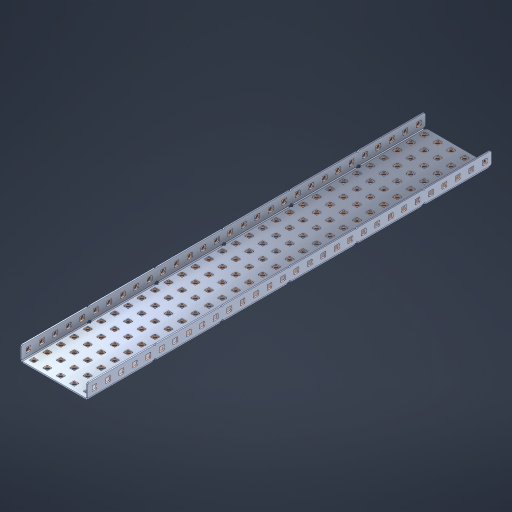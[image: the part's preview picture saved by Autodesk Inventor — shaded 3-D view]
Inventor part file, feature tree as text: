
AUTODESK INVENTOR PART (.ipt)
format: ipt  version: 2023 (Build 270158000, 158)  size: 2,276,864 bytes
history: native  units: in
note: dims shown in document units (in); Inventor stores cm internally (conversion verified against a paired STEP export)
features: other x215, extrude x209, sheet_metal_op x10, sketch x8, mirror x1, pattern_linear x1, chamfer x1
ambient origin geometry x8: Origin, YZ Plane, XZ Plane, XY Plane, X Axis, Y Axis, Z Axis, Center Point
bodies: Solid1 (feature_tree), Body (feature_tree)
feature tree (445):
  other  "Flange Pattern Plane"
  sheet_metal_op  "Flange Pattern"
  sheet_metal_op  "Body Pattern"
  other  "Arc Length"
  mirror  "Notch Mirror"
  pattern_linear  "Notch Pattern"  Spacing1=0.1875in  [1 undecoded]
  chamfer  "End Chamfer"
  extrude  "Half Cut"  Depth=0.0469in
  sketch  "Sketch1"  dims[d0=2.5in]
  other  "Plate1"
  sketch  "Sketch2"  dims[d1=15.0in]
  other  "Plate2"
  sheet_metal_op  "Bend1"
  sheet_metal_op  "Corner1"
  sketch  "Sketch3"  dims[d2=0.0469in]
  other  "Flange Pattern Sketch"
  sketch  "Sketch7"  dims[d3=0.0469in]
  other  "Srf1"
  other  "Srf2"
  sketch  "Sketch8"  dims[d4=0.0234in]
  sketch  "Sketch9"  dims[d5=0.0938in]
  other  "Srf91"
  sheet_metal_op  "Body Pattern Sketch"
  other  "Srf92"
  sketch  "Sketch13"  dims[d6=0.0469in]
  sketch  "Sketch14"  dims[d7=0.5in d8=90.0deg d9=0.0312in d10=0.1875in d11=0.0469in d12=0.0469in d16=0.182in d17=0.02in d18=0.0469in d19=0.0in d20=0.25in d21=0.25in d46=0.172in d47=1.0in d48=0.0in d49=0.182in d50=0.02in d51=0.25in d52=0.25in d53=0.0469in d54=0.0in d55=0.172in d56=1.0in d57=0.0in d60=11.811in d62=0.5in d63=1.9685in d65=0.5in d85=0.1227in d86=0.1659in d88=0.04in d89=0.0469in d90=0.0in d91=0.04in d92=0.0491in d95=2.5in d96=0.04in d97=0.25in d98=45.0deg d101=0.0in d102=2.497in d131=2.5in d132=11.811in d134=0.5in d139=0.5in]
  other  "Srf856"
  other  "Srf1310"
  other  "Srf1311"
  other  "Srf1312"
  other  "Srf1376"
  other  "Srf1377"
  other  "Srf1728"
  other  "Srf1755"
  other  "Srf1878"
  other  "Srf1879"
  other  "Srf1880"
  other  "Srf1881"
  other  "Srf1882"
  other  "Srf1883"
  other  "Srf1884"
  other  "Srf1885"
  other  "Srf1886"
  other  "Srf1887"
  other  "Srf1888"
  other  "Srf1889"
  other  "Srf1890"
  other  "Srf1891"
  other  "Srf1892"
  other  "Srf1893"
  other  "Srf1894"
  other  "Srf1895"
  other  "Srf1896"
  other  "Srf1897"
  other  "Srf1898"
  other  "Srf1899"
  other  "Srf1900"
  other  "Srf1901"
  other  "Srf1902"
  other  "Srf1903"
  other  "Srf1904"
  other  "Srf1905"
  other  "Srf1906"
  other  "Srf1942"
  other  "Srf1943"
  other  "Srf1944"
  other  "Srf1945"
  other  "Srf1946"
  other  "Srf1947"
  other  "Srf1948"
  other  "Srf1949"
  other  "Srf1950"
  other  "Srf1951"
  other  "Srf1952"
  other  "Srf1953"
  other  "Srf1954"
  other  "Srf1955"
  other  "Srf1956"
  other  "Srf1957"
  other  "Srf1958"
  other  "Srf1959"
  other  "Srf1960"
  other  "Srf1961"
  other  "Srf1962"
  other  "Srf1963"
  other  "Srf1964"
  other  "Srf1965"
  other  "Srf1966"
  other  "Srf1967"
  other  "Srf1968"
  other  "Srf1969"
  other  "Srf1970"
  other  "Srf2111"
  other  "Srf2112"
  other  "Srf2113"
  other  "Srf2114"
  other  "Srf2115"
  other  "Srf2116"
  other  "Srf2117"
  other  "Srf2118"
  other  "Srf2119"
  other  "Srf2120"
  other  "Srf2121"
  other  "Srf2122"
  other  "Srf2123"
  other  "Srf2124"
  other  "Srf2125"
  other  "Srf2126"
  other  "Srf2127"
  other  "Srf2128"
  other  "Srf2129"
  other  "Srf2130"
  other  "Srf2131"
  other  "Srf2132"
  other  "Srf2133"
  other  "Srf2134"
  other  "Srf2135"
  other  "Srf2146"
  other  "Srf2147"
  other  "Srf2148"
  other  "Srf2149"
  other  "Srf2150"
  other  "Srf2151"
  other  "Srf2152"
  other  "Srf2153"
  other  "Srf2154"
  other  "Srf2155"
  other  "Srf2156"
  other  "Srf2157"
  other  "Srf2158"
  other  "Srf2159"
  other  "Srf2160"
  other  "Srf2161"
  other  "Srf2162"
  other  "Srf2163"
  other  "Srf2164"
  other  "Srf2165"
  other  "Srf2166"
  other  "Srf2167"
  other  "Srf2168"
  other  "Srf2169"
  other  "Srf2170"
  other  "Srf2171"
  other  "Srf2172"
  other  "Srf2173"
  other  "Srf2174"
  other  "Srf2175"
  other  "Srf2176"
  other  "Srf2177"
  other  "Srf2178"
  other  "Srf2179"
  other  "Srf2180"
  other  "Srf2181"
  other  "Srf2182"
  other  "Srf2183"
  other  "Srf2184"
  other  "Srf2185"
  other  "Srf2186"
  other  "Srf2187"
  other  "Srf2188"
  other  "Srf2189"
  other  "Srf2190"
  other  "Srf2191"
  other  "Srf2192"
  other  "Srf2193"
  other  "Srf2194"
  other  "Srf2195"
  other  "Srf2196"
  other  "Srf2197"
  other  "Srf2198"
  other  "Srf2199"
  other  "Srf2200"
  other  "Srf2201"
  other  "Srf2202"
  other  "Srf2203"
  other  "Srf2204"
  other  "Srf2205"
  other  "Srf2206"
  other  "Srf2207"
  other  "Srf2208"
  other  "Srf2209"
  other  "Srf2210"
  other  "Srf2211"
  other  "Srf2212"
  other  "Srf2213"
  other  "Srf2214"
  other  "Srf2215"
  other  "Srf2216"
  other  "Srf2217"
  other  "Srf2218"
  other  "Srf2219"
  other  "Srf2220"
  other  "Srf2221"
  other  "Srf2222"
  other  "Srf2223"
  other  "Srf2224"
  other  "Srf2225"
  other  "Srf2226"
  other  "Srf2227"
  other  "Srf2228"
  other  "Srf2229"
  other  "Srf2230"
  other  "Srf2231"
  other  "Srf2232"
  other  "Srf2233"
  other  "Srf2234"
  other  "Srf2235"
  other  "Srf2236"
  other  "Srf2237"
  other  "Srf2238"
  other  "Srf2239"
  other  "Srf2240"
  other  "Srf2241"
  other  "Srf2242"
  other  "Srf2243"
  other  "Srf2244"
  other  "Srf2245"
  other  "Srf2246"
  other  "Srf2247"
  other  "Srf2248"
  other  "Srf2249"
  other  "Srf2250"
  other  "Srf2251"
  other  "Srf2252"
  other  "Srf2253"
  other  "Srf2254"
  other  "Srf2255"
  other  "Srf2256"
  other  "Srf2257"
  other  "Srf2258"
  other  "Srf2259"
  other  "Srf2260"
  sheet_metal_op  "Flange Stamp"
  sheet_metal_op  "Flange Circle"
  sheet_metal_op  "Body Stamp"
  sheet_metal_op  "Body Circle"
  sheet_metal_op  "Notch"
  extrude  "ExtrusionSrf2"  Depth=0.0469in
  extrude  "ExtrusionSrf92"  Depth=2.5in
  extrude  "ExtrusionSrf856"  Depth=0.02in
  extrude  "ExtrusionSrf1310"  Depth=0.0469in
  extrude  "ExtrusionSrf1311"  TaperAngle=0.0deg  [1 undecoded]
  extrude  "ExtrusionSrf1312"  Depth=0.25in
  extrude  "ExtrusionSrf1376"  Depth=0.25in
  extrude  "ExtrusionSrf1377"  Depth=2.5in
  extrude  "ExtrusionSrf1728"  Depth=2.5in TaperAngle=0.0deg
  extrude  "ExtrusionSrf1755"  Depth=2.5in
  extrude  "ExtrusionSrf1878"  Depth=0.02in
  extrude  "ExtrusionSrf1879"  Depth=0.25in
  extrude  "ExtrusionSrf1880"  Depth=0.25in
  extrude  "ExtrusionSrf1881"  Depth=0.0469in
  extrude  "ExtrusionSrf1882"  TaperAngle=0.0deg  [1 undecoded]
  extrude  "ExtrusionSrf1883"  Depth=2.5in
  extrude  "ExtrusionSrf1884"  Depth=2.5in TaperAngle=0.0deg
  extrude  "ExtrusionSrf1885"  Depth=2.5in
  extrude  "ExtrusionSrf1886"  Depth=2.5in
  extrude  "ExtrusionSrf1887"  Depth=2.5in
  extrude  "ExtrusionSrf1888"  Depth=2.5in
  extrude  "ExtrusionSrf1889"  Depth=2.5in
  extrude  "ExtrusionSrf1890"  Depth=0.0469in
  extrude  "ExtrusionSrf1891"  TaperAngle=0.0deg  [1 undecoded]
  extrude  "ExtrusionSrf1892"  Depth=2.5in
  extrude  "ExtrusionSrf1893"  Depth=2.5in
  extrude  "ExtrusionSrf1894"  Depth=2.5in
  extrude  "ExtrusionSrf1895"  Depth=0.25in TaperAngle=45.0deg
  extrude  "ExtrusionSrf1896"  TaperAngle=0.0deg  [1 undecoded]
  extrude  "ExtrusionSrf1897"  Depth=2.5in
  extrude  "ExtrusionSrf1898"  Depth=2.5in
  extrude  "ExtrusionSrf1899"  Depth=2.5in
  extrude  "ExtrusionSrf1900"  Depth=2.5in
  extrude  "ExtrusionSrf1901"  Depth=2.5in
  extrude  "ExtrusionSrf1902"  [1 undecoded]
  extrude  "ExtrusionSrf1903"  [1 undecoded]
  extrude  "ExtrusionSrf1904"  [1 undecoded]
  extrude  "ExtrusionSrf1905"  [1 undecoded]
  extrude  "ExtrusionSrf1906"  [1 undecoded]
  extrude  "ExtrusionSrf1942"  [1 undecoded]
  extrude  "ExtrusionSrf1943"  [1 undecoded]
  extrude  "ExtrusionSrf1944"  [1 undecoded]
  extrude  "ExtrusionSrf1945"  [1 undecoded]
  extrude  "ExtrusionSrf1946"  [1 undecoded]
  extrude  "ExtrusionSrf1947"  [1 undecoded]
  extrude  "ExtrusionSrf1948"  [1 undecoded]
  extrude  "ExtrusionSrf1949"  [1 undecoded]
  extrude  "ExtrusionSrf1950"  [1 undecoded]
  extrude  "ExtrusionSrf1951"  [1 undecoded]
  extrude  "ExtrusionSrf1952"  [1 undecoded]
  extrude  "ExtrusionSrf1953"  [1 undecoded]
  extrude  "ExtrusionSrf1954"  [1 undecoded]
  extrude  "ExtrusionSrf1955"  [1 undecoded]
  extrude  "ExtrusionSrf1956"  [1 undecoded]
  extrude  "ExtrusionSrf1957"  [1 undecoded]
  extrude  "ExtrusionSrf1958"  [1 undecoded]
  extrude  "ExtrusionSrf1959"  [1 undecoded]
  extrude  "ExtrusionSrf1960"  [1 undecoded]
  extrude  "ExtrusionSrf1961"  [1 undecoded]
  extrude  "ExtrusionSrf1962"  [1 undecoded]
  extrude  "ExtrusionSrf1963"  [1 undecoded]
  extrude  "ExtrusionSrf1964"  [1 undecoded]
  extrude  "ExtrusionSrf1965"  [1 undecoded]
  extrude  "ExtrusionSrf1966"  [1 undecoded]
  extrude  "ExtrusionSrf1967"  [1 undecoded]
  extrude  "ExtrusionSrf1968"  [1 undecoded]
  extrude  "ExtrusionSrf1969"  [1 undecoded]
  extrude  "ExtrusionSrf1970"  [1 undecoded]
  extrude  "ExtrusionSrf2111"  [1 undecoded]
  extrude  "ExtrusionSrf2112"  [1 undecoded]
  extrude  "ExtrusionSrf2113"  [1 undecoded]
  extrude  "ExtrusionSrf2114"  [1 undecoded]
  extrude  "ExtrusionSrf2115"  [1 undecoded]
  extrude  "ExtrusionSrf2116"  [1 undecoded]
  extrude  "ExtrusionSrf2117"  [1 undecoded]
  extrude  "ExtrusionSrf2118"  [1 undecoded]
  extrude  "ExtrusionSrf2119"  [1 undecoded]
  extrude  "ExtrusionSrf2120"  [1 undecoded]
  extrude  "ExtrusionSrf2121"  [1 undecoded]
  extrude  "ExtrusionSrf2122"  [1 undecoded]
  extrude  "ExtrusionSrf2123"  [1 undecoded]
  extrude  "ExtrusionSrf2124"  [1 undecoded]
  extrude  "ExtrusionSrf2125"  [1 undecoded]
  extrude  "ExtrusionSrf2126"  [1 undecoded]
  extrude  "ExtrusionSrf2127"  [1 undecoded]
  extrude  "ExtrusionSrf2128"  [1 undecoded]
  extrude  "ExtrusionSrf2129"  [1 undecoded]
  extrude  "ExtrusionSrf2130"  [1 undecoded]
  extrude  "ExtrusionSrf2131"  [1 undecoded]
  extrude  "ExtrusionSrf2132"  [1 undecoded]
  extrude  "ExtrusionSrf2133"  [1 undecoded]
  extrude  "ExtrusionSrf2134"  [1 undecoded]
  extrude  "ExtrusionSrf2135"  [1 undecoded]
  extrude  "ExtrusionSrf2146"  [1 undecoded]
  extrude  "ExtrusionSrf2147"  [1 undecoded]
  extrude  "ExtrusionSrf2148"  [1 undecoded]
  extrude  "ExtrusionSrf2149"  [1 undecoded]
  extrude  "ExtrusionSrf2150"  [1 undecoded]
  extrude  "ExtrusionSrf2151"  [1 undecoded]
  extrude  "ExtrusionSrf2152"  [1 undecoded]
  extrude  "ExtrusionSrf2153"  [1 undecoded]
  extrude  "ExtrusionSrf2154"  [1 undecoded]
  extrude  "ExtrusionSrf2155"  [1 undecoded]
  extrude  "ExtrusionSrf2156"  [1 undecoded]
  extrude  "ExtrusionSrf2157"  [1 undecoded]
  extrude  "ExtrusionSrf2158"  [1 undecoded]
  extrude  "ExtrusionSrf2159"  [1 undecoded]
  extrude  "ExtrusionSrf2160"  [1 undecoded]
  extrude  "ExtrusionSrf2161"  [1 undecoded]
  extrude  "ExtrusionSrf2162"  [1 undecoded]
  extrude  "ExtrusionSrf2163"  [1 undecoded]
  extrude  "ExtrusionSrf2164"  [1 undecoded]
  extrude  "ExtrusionSrf2165"  [1 undecoded]
  extrude  "ExtrusionSrf2166"  [1 undecoded]
  extrude  "ExtrusionSrf2167"  [1 undecoded]
  extrude  "ExtrusionSrf2168"  [1 undecoded]
  extrude  "ExtrusionSrf2169"  [1 undecoded]
  extrude  "ExtrusionSrf2170"  [1 undecoded]
  extrude  "ExtrusionSrf2171"  [1 undecoded]
  extrude  "ExtrusionSrf2172"  [1 undecoded]
  extrude  "ExtrusionSrf2173"  [1 undecoded]
  extrude  "ExtrusionSrf2174"  [1 undecoded]
  extrude  "ExtrusionSrf2175"  [1 undecoded]
  extrude  "ExtrusionSrf2176"  [1 undecoded]
  extrude  "ExtrusionSrf2177"  [1 undecoded]
  extrude  "ExtrusionSrf2178"  [1 undecoded]
  extrude  "ExtrusionSrf2179"  [1 undecoded]
  extrude  "ExtrusionSrf2180"  [1 undecoded]
  extrude  "ExtrusionSrf2181"  [1 undecoded]
  extrude  "ExtrusionSrf2182"  [1 undecoded]
  extrude  "ExtrusionSrf2183"  [1 undecoded]
  extrude  "ExtrusionSrf2184"  [1 undecoded]
  extrude  "ExtrusionSrf2185"  [1 undecoded]
  extrude  "ExtrusionSrf2186"  [1 undecoded]
  extrude  "ExtrusionSrf2187"  [1 undecoded]
  extrude  "ExtrusionSrf2188"  [1 undecoded]
  extrude  "ExtrusionSrf2189"  [1 undecoded]
  extrude  "ExtrusionSrf2190"  [1 undecoded]
  extrude  "ExtrusionSrf2191"  [1 undecoded]
  extrude  "ExtrusionSrf2192"  [1 undecoded]
  extrude  "ExtrusionSrf2193"  [1 undecoded]
  extrude  "ExtrusionSrf2194"  [1 undecoded]
  extrude  "ExtrusionSrf2195"  [1 undecoded]
  extrude  "ExtrusionSrf2196"  [1 undecoded]
  extrude  "ExtrusionSrf2197"  [1 undecoded]
  extrude  "ExtrusionSrf2198"  [1 undecoded]
  extrude  "ExtrusionSrf2199"  [1 undecoded]
  extrude  "ExtrusionSrf2200"  [1 undecoded]
  extrude  "ExtrusionSrf2201"  [1 undecoded]
  extrude  "ExtrusionSrf2202"  [1 undecoded]
  extrude  "ExtrusionSrf2203"  [1 undecoded]
  extrude  "ExtrusionSrf2204"  [1 undecoded]
  extrude  "ExtrusionSrf2205"  [1 undecoded]
  extrude  "ExtrusionSrf2206"  [1 undecoded]
  extrude  "ExtrusionSrf2207"  [1 undecoded]
  extrude  "ExtrusionSrf2208"  [1 undecoded]
  extrude  "ExtrusionSrf2209"  [1 undecoded]
  extrude  "ExtrusionSrf2210"  [1 undecoded]
  extrude  "ExtrusionSrf2211"  [1 undecoded]
  extrude  "ExtrusionSrf2212"  [1 undecoded]
  extrude  "ExtrusionSrf2213"  [1 undecoded]
  extrude  "ExtrusionSrf2214"  [1 undecoded]
  extrude  "ExtrusionSrf2215"  [1 undecoded]
  extrude  "ExtrusionSrf2216"  [1 undecoded]
  extrude  "ExtrusionSrf2217"  [1 undecoded]
  extrude  "ExtrusionSrf2218"  [1 undecoded]
  extrude  "ExtrusionSrf2219"  [1 undecoded]
  extrude  "ExtrusionSrf2220"  [1 undecoded]
  extrude  "ExtrusionSrf2221"  [1 undecoded]
  extrude  "ExtrusionSrf2222"  [1 undecoded]
  extrude  "ExtrusionSrf2223"  [1 undecoded]
  extrude  "ExtrusionSrf2224"  [1 undecoded]
  extrude  "ExtrusionSrf2225"  [1 undecoded]
  extrude  "ExtrusionSrf2226"  [1 undecoded]
  extrude  "ExtrusionSrf2227"  [1 undecoded]
  extrude  "ExtrusionSrf2228"  [1 undecoded]
  extrude  "ExtrusionSrf2229"  [1 undecoded]
  extrude  "ExtrusionSrf2230"  [1 undecoded]
  extrude  "ExtrusionSrf2231"  [1 undecoded]
  extrude  "ExtrusionSrf2232"  [1 undecoded]
  extrude  "ExtrusionSrf2233"  [1 undecoded]
  extrude  "ExtrusionSrf2234"  [1 undecoded]
  extrude  "ExtrusionSrf2235"  [1 undecoded]
  extrude  "ExtrusionSrf2236"  [1 undecoded]
  extrude  "ExtrusionSrf2237"  [1 undecoded]
  extrude  "ExtrusionSrf2238"  [1 undecoded]
  extrude  "ExtrusionSrf2239"  [1 undecoded]
  extrude  "ExtrusionSrf2240"  [1 undecoded]
  extrude  "ExtrusionSrf2241"  [1 undecoded]
  extrude  "ExtrusionSrf2242"  [1 undecoded]
  extrude  "ExtrusionSrf2243"  [1 undecoded]
  extrude  "ExtrusionSrf2244"  [1 undecoded]
  extrude  "ExtrusionSrf2245"  [1 undecoded]
  extrude  "ExtrusionSrf2246"  [1 undecoded]
  extrude  "ExtrusionSrf2247"  [1 undecoded]
  extrude  "ExtrusionSrf2248"  [1 undecoded]
  extrude  "ExtrusionSrf2249"  [1 undecoded]
  extrude  "ExtrusionSrf2250"  [1 undecoded]
  extrude  "ExtrusionSrf2251"  [1 undecoded]
  extrude  "ExtrusionSrf2252"  [1 undecoded]
  extrude  "ExtrusionSrf2253"  [1 undecoded]
  extrude  "ExtrusionSrf2254"  [1 undecoded]
  extrude  "ExtrusionSrf2255"  [1 undecoded]
  extrude  "ExtrusionSrf2256"  [1 undecoded]
  extrude  "ExtrusionSrf2257"  [1 undecoded]
  extrude  "ExtrusionSrf2258"  [1 undecoded]
  extrude  "ExtrusionSrf2259"  [1 undecoded]
  extrude  "ExtrusionSrf2260"  [1 undecoded]
note: 179 required parameter values undecoded (feature->parameter linkage not recoverable at this tier; creation-order binding heuristic only, values carry confidence <= 0.55)
